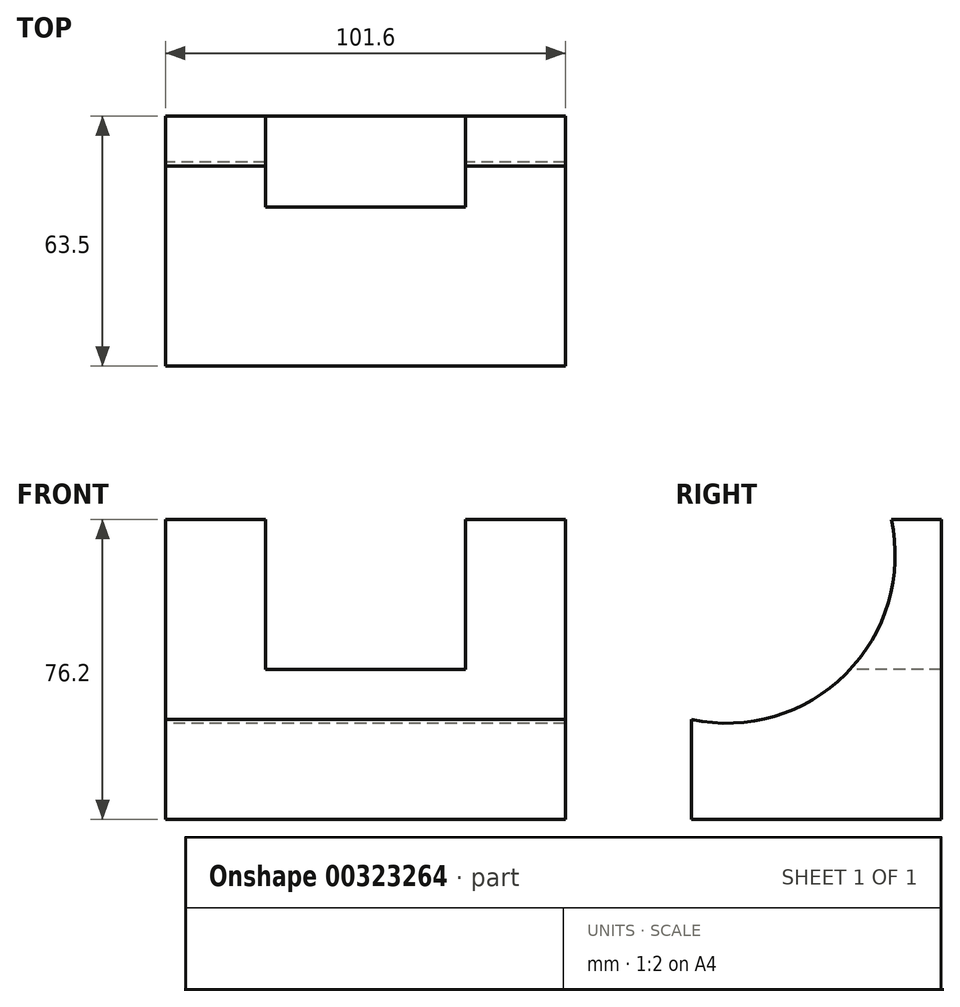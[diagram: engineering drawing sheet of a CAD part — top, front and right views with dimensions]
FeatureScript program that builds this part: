
annotation { "Feature Type Name" : "Feature", "Feature Type Description" : "" }
export const myFeature = defineFeature(function(context is Context, id is Id, definition is map)
    precondition{}
    {
        {
            var Q0;
            Q0=qCreatedBy(makeId("Front.planeOp"),FACE);
            var sketch = newSketch(context, id + "F0", { "sketchPlane" : qUnion([Q0])});
            skLineSegment(sketch, "E0", {"start": v(-51.07, -40.4) * mm, "end": v(50.53, -40.4) * mm});
            skLineSegment(sketch, "E1", {"start": v(-51.07, -40.4) * mm, "end": v(-51.07, 35.8) * mm});
            skLineSegment(sketch, "E2", {"start": v(-51.07, 35.8) * mm, "end": v(50.53, 35.8) * mm});
            skLineSegment(sketch, "E3", {"start": v(50.53, 35.8) * mm, "end": v(50.53, -40.4) * mm});
            skSolve(sketch);
        }
        {
            var Q0;
            Q0 = qSketchRegion(id + "F0", true);
            extrude(context, id + "F1", {"entities" : qUnion([Q0]), "depth" : 63.5 * mm});
        }
        {
            var Q0;
            Q0=makeQuery(id+"F1.opExtrude","SWEPT_FACE",FACE,{"disambiguationData":[OSD([sQuery(id+"F0.wireOp",EDGE,"E1")])]});
            var sketch = newSketch(context, id + "F2", { "sketchPlane" : qUnion([Q0])});
            skArc(sketch, "E4", {"start": v(12.7, 35.8) * mm, "mid": v(24.27, -3.42) * mm, "end": v(63.5, -15) * mm});
            skSolve(sketch);
        }
        {
            var Q0;
            Q0 = qSketchRegion(id + "F2", true);
            var Q1;
            {var subQ0=sQuery(id+"F2.wireOp",EDGE,"E4");Q1=makeQuery(id+"F2.imprint","IMPRINT",FACE,{"disambiguationData":[TD([[makeQuery(id+"F2.imprint","IMPRINT",EDGE,{"derivedFrom":subQ0}),1.0]])]});}
            extrude(context, id + "F3", {"entities" : qUnion([Q0, Q1]), "operationType" : NewBodyOperationType.REMOVE, "oppositeDirection" : true, "depth" : 101.6 * mm});
        }
        {
            var Q0;
            Q0=makeQuery(id+"F1.opExtrude","SWEPT_FACE",FACE,{"disambiguationData":[OSD([sQuery(id+"F0.wireOp",EDGE,"E2")])]});
            var sketch = newSketch(context, id + "F4", { "sketchPlane" : qUnion([Q0])});
            skLineSegment(sketch, "E5", {"start": v(-25.67, 0) * mm, "end": v(-25.67, -12.7) * mm});
            skLineSegment(sketch, "E6", {"start": v(-25.67, -12.7) * mm, "end": v(25.13, -12.7) * mm});
            skLineSegment(sketch, "E7", {"start": v(25.13, -12.7) * mm, "end": v(25.13, 0) * mm});
            skLineSegment(sketch, "E8", {"start": v(25.13, 0) * mm, "end": v(-25.67, 0) * mm});
            skSolve(sketch);
        }
        {
            var Q0;
            Q0=makeQuery(id+"F4.imprint","IMPRINT",FACE,{"disambiguationData":[TD([[makeQuery(id+"F4.imprint","IMPRINT",EDGE,{"derivedFrom":sQuery(id+"F4.wireOp",EDGE,"E5")}),1.0]])]});
            extrude(context, id + "F5", {"entities" : qUnion([Q0]), "operationType" : NewBodyOperationType.REMOVE, "oppositeDirection" : true, "depth" : 38.1 * mm});
        }
        {
            var Q0;
            Q0=makeQuery(id+"F5.boolean.opBoolean","COPY",FACE,{"derivedFrom":makeQuery(id+"F5.opExtrude","SWEPT_FACE",FACE,{"disambiguationData":[OSD([sQuery(id+"F4.wireOp",EDGE,"E6")])]})});
            extrude(context, id + "F6", {"entities" : qUnion([Q0]), "operationType" : NewBodyOperationType.REMOVE, "oppositeDirection" : true, "depth" : 25.4 * mm});
        }
    });
